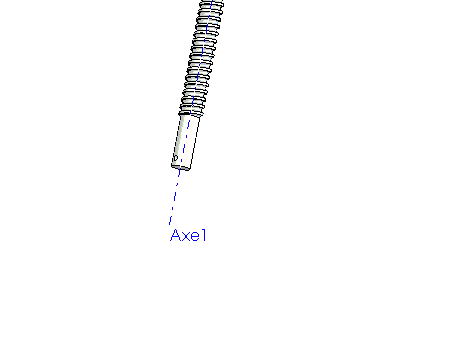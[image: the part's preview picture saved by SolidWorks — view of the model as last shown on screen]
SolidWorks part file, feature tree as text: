
SOLIDWORKS PART (.sldprt)
format: sldprt  version: not decoded by parser v0  size: 9,963,008 bytes
history: native  units: mm
features: sketch x7, extrude x4, plane x3, material x1, helix x1, cut_extrude x1, sweep x1 + 1 further entry (+7 scaffold rows collapsed)
feature tree (26):
  scaffold x7  (default folders/planes/origin — collapsed)
  material  "Matériau <non spécifié>"
  "Corps de surface"
  plane  "Face"
  plane  "Dessus"
  plane  "Droite"
  sketch  "Esquisse1"  dims[D1=6.0mm]
  extrude  "Extrusion1"  Depth=26.5mm
  sketch  "Esquisse2"  dims[D1=5.0mm]
  extrude  "Extrusion2"  Depth=1.5mm
  sketch  "Esquisse3"  dims[D1=9.5mm]
  extrude  "Extrusion3"  Depth=310mm
  sketch  "Esquisse4"  dims[D1=~2.379768mm]
  extrude  "Extrusion4"  Depth=21mm
  sketch  "Esquisse5"  dims[D1=9.5mm]
  helix  "Hélice1"  Pitch=312mm
  sketch  "Esquisse6"  dims[D1=2.0mm]
  sketch  "Esquisse8"  dims[c1.D1=2.0mm c1.D2=~1.735111mm c2.D1=3.0mm c2.D2=2.0mm]
  cut_extrude  "Enlèv. mat.-Extru.1"  Depth=10mm
  sweep  "Enlèvement de matière-Balayage1"
decode coverage: 13 of 14 modeling features carry decoded parameters; 1 rows unclassified (native names shown)
note: ~ marks probable driven/reference dimensions
note: suppression state not decoded; provenance and decode notes live in map.json
